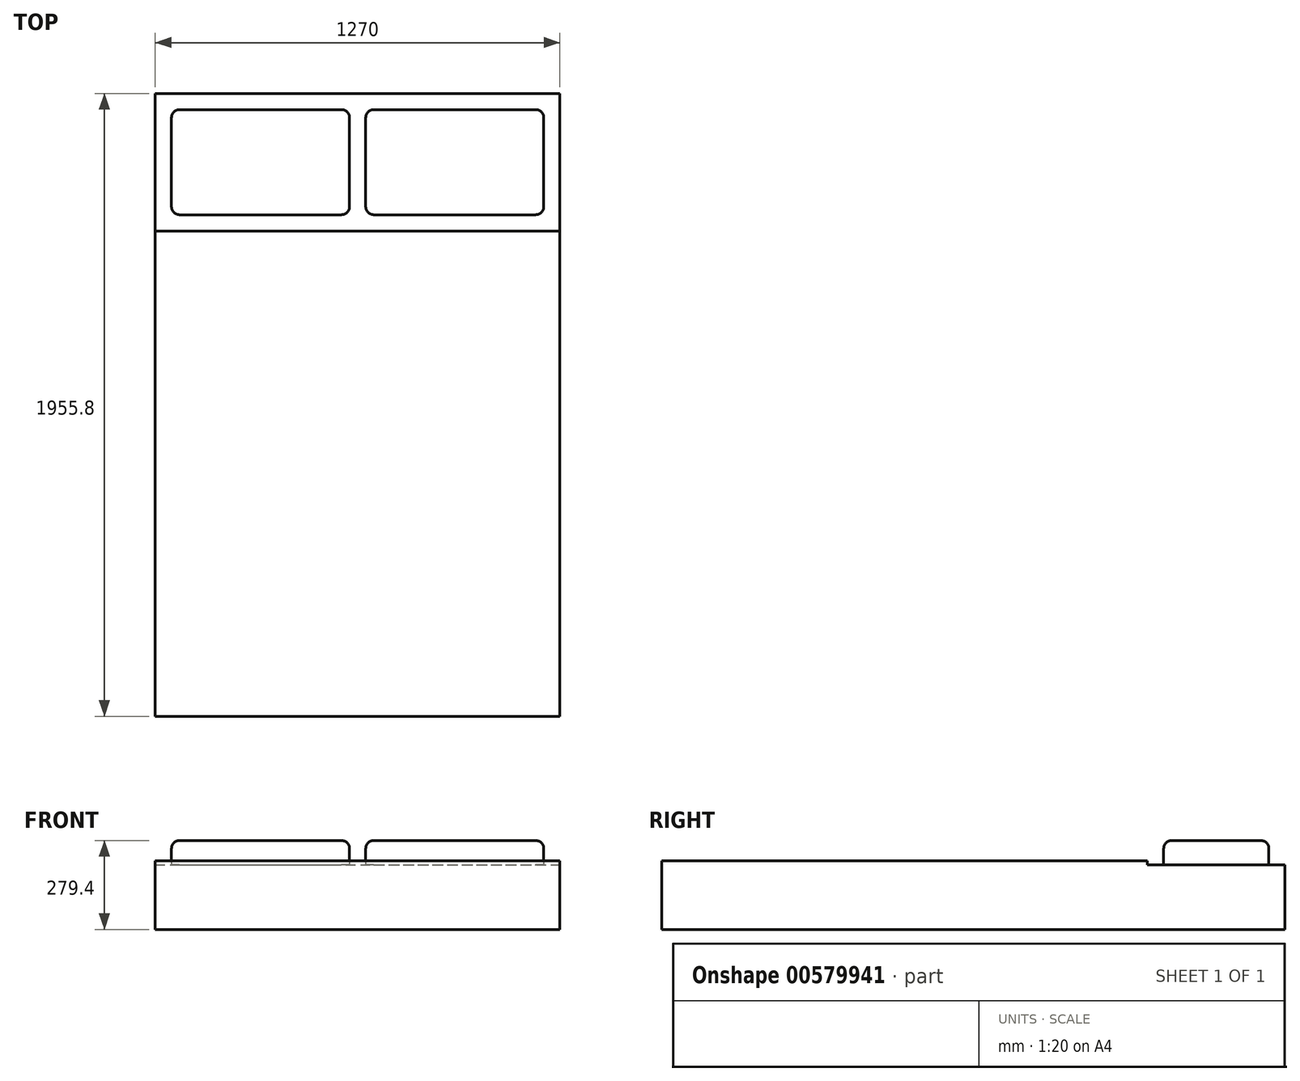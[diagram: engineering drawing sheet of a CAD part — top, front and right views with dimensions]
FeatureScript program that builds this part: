
annotation { "Feature Type Name" : "Feature", "Feature Type Description" : "" }
export const myFeature = defineFeature(function(context is Context, id is Id, definition is map)
    precondition{}
    {
        {
            var Q0;
            Q0=qCreatedBy(makeId("Top.planeOp"),FACE);
            var sketch = newSketch(context, id + "F0", { "sketchPlane" : qUnion([Q0])});
            skLineSegment(sketch, "E0.bottom", {"start": v(-642.09, 1077.96) * mm, "end": v(627.91, 1077.96) * mm});
            skLineSegment(sketch, "E0.top", {"start": v(-642.09, -877.84) * mm, "end": v(627.91, -877.84) * mm});
            skLineSegment(sketch, "E0.left", {"start": v(-642.09, 1077.96) * mm, "end": v(-642.09, -877.84) * mm});
            skLineSegment(sketch, "E0.right", {"start": v(627.91, 1077.96) * mm, "end": v(627.91, -877.84) * mm});
            skSolve(sketch);
        }
        {
            var Q0;
            Q0=makeQuery(id+"F0.imprint","IMPRINT",FACE,{"disambiguationData":[TD([[makeQuery(id+"F0.imprint","IMPRINT",EDGE,{"derivedFrom":sQuery(id+"F0.wireOp",EDGE,"E0.bottom")}),-1.0]])]});
            extrude(context, id + "F1", {"entities" : qUnion([Q0]), "depth" : 203.2 * mm, "offsetDistance" : 25.4 * mm});
        }
        {
            var Q0;
            Q0=makeQuery(id+"F1.opExtrude","CAP_FACE",FACE,{"disambiguationData":[OSD([sQuery(id+"F0.wireOp",EDGE,"E0.bottom"),sQuery(id+"F0.wireOp",EDGE,"E0.top"),sQuery(id+"F0.wireOp",EDGE,"E0.left"),sQuery(id+"F0.wireOp",EDGE,"E0.right")])],"isStart":false});
            var sketch = newSketch(context, id + "F2", { "sketchPlane" : qUnion([Q0])});
            skLineSegment(sketch, "E1.bottom", {"start": v(-642.09, -877.84) * mm, "end": v(627.91, -877.84) * mm});
            skLineSegment(sketch, "E1.top", {"start": v(-642.09, 646.16) * mm, "end": v(627.91, 646.16) * mm});
            skLineSegment(sketch, "E1.left", {"start": v(-642.09, -877.84) * mm, "end": v(-642.09, 646.16) * mm});
            skLineSegment(sketch, "E1.right", {"start": v(627.91, -877.84) * mm, "end": v(627.91, 646.16) * mm});
            skSolve(sketch);
        }
        {
            var Q0;
            Q0=makeQuery(id+"F2.imprint","IMPRINT",FACE,{"disambiguationData":[TD([[makeQuery(id+"F2.imprint","IMPRINT",EDGE,{"derivedFrom":sQuery(id+"F2.wireOp",EDGE,"E1.bottom")}),1.0]])]});
            extrude(context, id + "F3", {"entities" : qUnion([Q0]), "operationType" : NewBodyOperationType.ADD, "depth" : 12.7 * mm, "offsetDistance" : 25.4 * mm});
        }
        {
            var Q0;
            Q0=makeQuery(id+"F1.opExtrude","CAP_FACE",FACE,{"disambiguationData":[OSD([sQuery(id+"F0.wireOp",EDGE,"E0.bottom"),sQuery(id+"F0.wireOp",EDGE,"E0.top"),sQuery(id+"F0.wireOp",EDGE,"E0.left"),sQuery(id+"F0.wireOp",EDGE,"E0.right")])],"isStart":false});
            var sketch = newSketch(context, id + "F4", { "sketchPlane" : qUnion([Q0])});
            skLineSegment(sketch, "E2.bottom", {"start": v(-591.29, 1027.16) * mm, "end": v(-32.49, 1027.16) * mm});
            skLineSegment(sketch, "E2.top", {"start": v(-591.29, 696.96) * mm, "end": v(-32.49, 696.96) * mm});
            skLineSegment(sketch, "E2.left", {"start": v(-591.29, 1027.16) * mm, "end": v(-591.29, 696.96) * mm});
            skLineSegment(sketch, "E2.right", {"start": v(-32.49, 1027.16) * mm, "end": v(-32.49, 696.96) * mm});
            skLineSegment(sketch, "E3.bottom", {"start": v(18.31, 1027.16) * mm, "end": v(577.11, 1027.16) * mm});
            skLineSegment(sketch, "E3.top", {"start": v(18.31, 696.96) * mm, "end": v(577.11, 696.96) * mm});
            skLineSegment(sketch, "E3.left", {"start": v(18.31, 1027.16) * mm, "end": v(18.31, 696.96) * mm});
            skLineSegment(sketch, "E3.right", {"start": v(577.11, 1027.16) * mm, "end": v(577.11, 696.96) * mm});
            skSolve(sketch);
        }
        {
            var Q0;
            Q0 = qSketchRegion(id + "F4", true);
            extrude(context, id + "F5", {"entities" : qUnion([Q0]), "operationType" : NewBodyOperationType.ADD, "depth" : 76.2 * mm, "offsetDistance" : 25.4 * mm});
        }
        {
            var Q0;
            Q0=makeQuery(id+"F5.opExtrude","SWEPT_EDGE",EDGE,{"disambiguationData":[OSD([sQuery(id+"F4.wireOp",EDGE,"E2.bottom"),sQuery(id+"F4.wireOp",EDGE,"E2.right")])]});
            var Q1;
            Q1=makeQuery(id+"F5.opExtrude","SWEPT_EDGE",EDGE,{"disambiguationData":[OSD([sQuery(id+"F4.wireOp",EDGE,"E2.top"),sQuery(id+"F4.wireOp",EDGE,"E2.right")])]});
            var Q2;
            Q2=makeQuery(id+"F5.opExtrude","SWEPT_EDGE",EDGE,{"disambiguationData":[OSD([sQuery(id+"F4.wireOp",EDGE,"E3.top"),sQuery(id+"F4.wireOp",EDGE,"E3.left")])]});
            var Q3;
            Q3=makeQuery(id+"F5.opExtrude","SWEPT_EDGE",EDGE,{"disambiguationData":[OSD([sQuery(id+"F4.wireOp",EDGE,"E3.bottom"),sQuery(id+"F4.wireOp",EDGE,"E3.left")])]});
            var Q4;
            Q4=makeQuery(id+"F5.opExtrude","SWEPT_EDGE",EDGE,{"disambiguationData":[OSD([sQuery(id+"F4.wireOp",EDGE,"E3.top"),sQuery(id+"F4.wireOp",EDGE,"E3.right")])]});
            var Q5;
            Q5=makeQuery(id+"F5.opExtrude","SWEPT_EDGE",EDGE,{"disambiguationData":[OSD([sQuery(id+"F4.wireOp",EDGE,"E3.bottom"),sQuery(id+"F4.wireOp",EDGE,"E3.right")])]});
            var Q6;
            Q6=makeQuery(id+"F5.opExtrude","SWEPT_EDGE",EDGE,{"disambiguationData":[OSD([sQuery(id+"F4.wireOp",EDGE,"E2.bottom"),sQuery(id+"F4.wireOp",EDGE,"E2.left")])]});
            var Q7;
            Q7=makeQuery(id+"F5.opExtrude","SWEPT_EDGE",EDGE,{"disambiguationData":[OSD([sQuery(id+"F4.wireOp",EDGE,"E2.top"),sQuery(id+"F4.wireOp",EDGE,"E2.left")])]});
            fillet(context, id + "F6", {"entities" : qUnion([Q0, Q1, Q2, Q3, Q4, Q5, Q6, Q7]), "radius" : 25.4 * mm, "tangentPropagation" : true, "allowEdgeOverflow" : false});
        }
        {
            var Q0;
            Q0=makeQuery(id+"F5.opExtrude","CAP_EDGE",EDGE,{"disambiguationData":[OSD([sQuery(id+"F4.wireOp",EDGE,"E2.bottom")])],"isStart":false});
            var Q1;
            Q1=makeQuery(id+"F5.opExtrude","CAP_EDGE",EDGE,{"disambiguationData":[OSD([sQuery(id+"F4.wireOp",EDGE,"E2.right")])],"isStart":false});
            var Q2;
            {var subQ0=sQuery(id+"F4.wireOp",EDGE,"E2.right");var subQ1=sQuery(id+"F4.wireOp",EDGE,"E2.bottom");Q2=makeQuery(id+"F6.opFillet","BLEND_EDGE",EDGE,{"blendedFrom":[makeQuery(id+"F5.opExtrude","SWEPT_EDGE",EDGE,{"disambiguationData":[OSD([subQ1,subQ0])]}),makeQuery(id+"F5.opExtrude","CAP_FACE",FACE,{"disambiguationData":[OSD([subQ1,sQuery(id+"F4.wireOp",EDGE,"E2.top"),sQuery(id+"F4.wireOp",EDGE,"E2.left"),subQ0])],"isStart":false})],"blendedInto":[makeQuery(id+"F5.opExtrude","CAP_FACE",FACE,{"disambiguationData":[OSD([subQ1,sQuery(id+"F4.wireOp",EDGE,"E2.top"),sQuery(id+"F4.wireOp",EDGE,"E2.left"),subQ0])],"isStart":false})]});}
            var Q3;
            {var subQ0=sQuery(id+"F4.wireOp",EDGE,"E2.right");var subQ1=sQuery(id+"F4.wireOp",EDGE,"E2.top");Q3=makeQuery(id+"F6.opFillet","BLEND_EDGE",EDGE,{"blendedFrom":[makeQuery(id+"F5.opExtrude","SWEPT_EDGE",EDGE,{"disambiguationData":[OSD([subQ1,subQ0])]}),makeQuery(id+"F5.opExtrude","CAP_FACE",FACE,{"disambiguationData":[OSD([sQuery(id+"F4.wireOp",EDGE,"E2.bottom"),subQ1,sQuery(id+"F4.wireOp",EDGE,"E2.left"),subQ0])],"isStart":false})],"blendedInto":[makeQuery(id+"F5.opExtrude","CAP_FACE",FACE,{"disambiguationData":[OSD([sQuery(id+"F4.wireOp",EDGE,"E2.bottom"),subQ1,sQuery(id+"F4.wireOp",EDGE,"E2.left"),subQ0])],"isStart":false})]});}
            var Q4;
            Q4=makeQuery(id+"F5.opExtrude","CAP_EDGE",EDGE,{"disambiguationData":[OSD([sQuery(id+"F4.wireOp",EDGE,"E2.top")])],"isStart":false});
            var Q5;
            {var subQ0=sQuery(id+"F4.wireOp",EDGE,"E2.left");var subQ1=sQuery(id+"F4.wireOp",EDGE,"E2.top");Q5=makeQuery(id+"F6.opFillet","BLEND_EDGE",EDGE,{"blendedFrom":[makeQuery(id+"F5.opExtrude","SWEPT_EDGE",EDGE,{"disambiguationData":[OSD([subQ1,subQ0])]}),makeQuery(id+"F5.opExtrude","CAP_FACE",FACE,{"disambiguationData":[OSD([sQuery(id+"F4.wireOp",EDGE,"E2.bottom"),subQ1,subQ0,sQuery(id+"F4.wireOp",EDGE,"E2.right")])],"isStart":false})],"blendedInto":[makeQuery(id+"F5.opExtrude","CAP_FACE",FACE,{"disambiguationData":[OSD([sQuery(id+"F4.wireOp",EDGE,"E2.bottom"),subQ1,subQ0,sQuery(id+"F4.wireOp",EDGE,"E2.right")])],"isStart":false})]});}
            var Q6;
            Q6=makeQuery(id+"F5.opExtrude","CAP_EDGE",EDGE,{"disambiguationData":[OSD([sQuery(id+"F4.wireOp",EDGE,"E2.left")])],"isStart":false});
            var Q7;
            {var subQ0=sQuery(id+"F4.wireOp",EDGE,"E2.left");var subQ1=sQuery(id+"F4.wireOp",EDGE,"E2.bottom");Q7=makeQuery(id+"F6.opFillet","BLEND_EDGE",EDGE,{"blendedFrom":[makeQuery(id+"F5.opExtrude","SWEPT_EDGE",EDGE,{"disambiguationData":[OSD([subQ1,subQ0])]}),makeQuery(id+"F5.opExtrude","CAP_FACE",FACE,{"disambiguationData":[OSD([subQ1,sQuery(id+"F4.wireOp",EDGE,"E2.top"),subQ0,sQuery(id+"F4.wireOp",EDGE,"E2.right")])],"isStart":false})],"blendedInto":[makeQuery(id+"F5.opExtrude","CAP_FACE",FACE,{"disambiguationData":[OSD([subQ1,sQuery(id+"F4.wireOp",EDGE,"E2.top"),subQ0,sQuery(id+"F4.wireOp",EDGE,"E2.right")])],"isStart":false})]});}
            var Q8;
            Q8=makeQuery(id+"F5.opExtrude","CAP_EDGE",EDGE,{"disambiguationData":[OSD([sQuery(id+"F4.wireOp",EDGE,"E3.left")])],"isStart":false});
            var Q9;
            {var subQ0=sQuery(id+"F4.wireOp",EDGE,"E3.left");var subQ1=sQuery(id+"F4.wireOp",EDGE,"E3.bottom");Q9=makeQuery(id+"F6.opFillet","BLEND_EDGE",EDGE,{"blendedFrom":[makeQuery(id+"F5.opExtrude","SWEPT_EDGE",EDGE,{"disambiguationData":[OSD([subQ1,subQ0])]}),makeQuery(id+"F5.opExtrude","CAP_FACE",FACE,{"disambiguationData":[OSD([subQ1,sQuery(id+"F4.wireOp",EDGE,"E3.top"),subQ0,sQuery(id+"F4.wireOp",EDGE,"E3.right")])],"isStart":false})],"blendedInto":[makeQuery(id+"F5.opExtrude","CAP_FACE",FACE,{"disambiguationData":[OSD([subQ1,sQuery(id+"F4.wireOp",EDGE,"E3.top"),subQ0,sQuery(id+"F4.wireOp",EDGE,"E3.right")])],"isStart":false})]});}
            var Q10;
            Q10=makeQuery(id+"F5.opExtrude","CAP_EDGE",EDGE,{"disambiguationData":[OSD([sQuery(id+"F4.wireOp",EDGE,"E3.bottom")])],"isStart":false});
            var Q11;
            {var subQ0=sQuery(id+"F4.wireOp",EDGE,"E3.right");var subQ1=sQuery(id+"F4.wireOp",EDGE,"E3.bottom");Q11=makeQuery(id+"F6.opFillet","BLEND_EDGE",EDGE,{"blendedFrom":[makeQuery(id+"F5.opExtrude","SWEPT_EDGE",EDGE,{"disambiguationData":[OSD([subQ1,subQ0])]}),makeQuery(id+"F5.opExtrude","CAP_FACE",FACE,{"disambiguationData":[OSD([subQ1,sQuery(id+"F4.wireOp",EDGE,"E3.top"),sQuery(id+"F4.wireOp",EDGE,"E3.left"),subQ0])],"isStart":false})],"blendedInto":[makeQuery(id+"F5.opExtrude","CAP_FACE",FACE,{"disambiguationData":[OSD([subQ1,sQuery(id+"F4.wireOp",EDGE,"E3.top"),sQuery(id+"F4.wireOp",EDGE,"E3.left"),subQ0])],"isStart":false})]});}
            var Q12;
            Q12=makeQuery(id+"F5.opExtrude","CAP_EDGE",EDGE,{"disambiguationData":[OSD([sQuery(id+"F4.wireOp",EDGE,"E3.right")])],"isStart":false});
            var Q13;
            {var subQ0=sQuery(id+"F4.wireOp",EDGE,"E3.right");var subQ1=sQuery(id+"F4.wireOp",EDGE,"E3.top");Q13=makeQuery(id+"F6.opFillet","BLEND_EDGE",EDGE,{"blendedFrom":[makeQuery(id+"F5.opExtrude","SWEPT_EDGE",EDGE,{"disambiguationData":[OSD([subQ1,subQ0])]}),makeQuery(id+"F5.opExtrude","CAP_FACE",FACE,{"disambiguationData":[OSD([sQuery(id+"F4.wireOp",EDGE,"E3.bottom"),subQ1,sQuery(id+"F4.wireOp",EDGE,"E3.left"),subQ0])],"isStart":false})],"blendedInto":[makeQuery(id+"F5.opExtrude","CAP_FACE",FACE,{"disambiguationData":[OSD([sQuery(id+"F4.wireOp",EDGE,"E3.bottom"),subQ1,sQuery(id+"F4.wireOp",EDGE,"E3.left"),subQ0])],"isStart":false})]});}
            var Q14;
            Q14=makeQuery(id+"F5.opExtrude","CAP_EDGE",EDGE,{"disambiguationData":[OSD([sQuery(id+"F4.wireOp",EDGE,"E3.top")])],"isStart":false});
            var Q15;
            {var subQ0=sQuery(id+"F4.wireOp",EDGE,"E3.left");var subQ1=sQuery(id+"F4.wireOp",EDGE,"E3.top");Q15=makeQuery(id+"F6.opFillet","BLEND_EDGE",EDGE,{"blendedFrom":[makeQuery(id+"F5.opExtrude","SWEPT_EDGE",EDGE,{"disambiguationData":[OSD([subQ1,subQ0])]}),makeQuery(id+"F5.opExtrude","CAP_FACE",FACE,{"disambiguationData":[OSD([sQuery(id+"F4.wireOp",EDGE,"E3.bottom"),subQ1,subQ0,sQuery(id+"F4.wireOp",EDGE,"E3.right")])],"isStart":false})],"blendedInto":[makeQuery(id+"F5.opExtrude","CAP_FACE",FACE,{"disambiguationData":[OSD([sQuery(id+"F4.wireOp",EDGE,"E3.bottom"),subQ1,subQ0,sQuery(id+"F4.wireOp",EDGE,"E3.right")])],"isStart":false})]});}
            fillet(context, id + "F7", {"entities" : qUnion([Q0, Q1, Q2, Q3, Q4, Q5, Q6, Q7, Q8, Q9, Q10, Q11, Q12, Q13, Q14, Q15]), "radius" : 25.4 * mm, "tangentPropagation" : true, "allowEdgeOverflow" : false});
        }
    });
